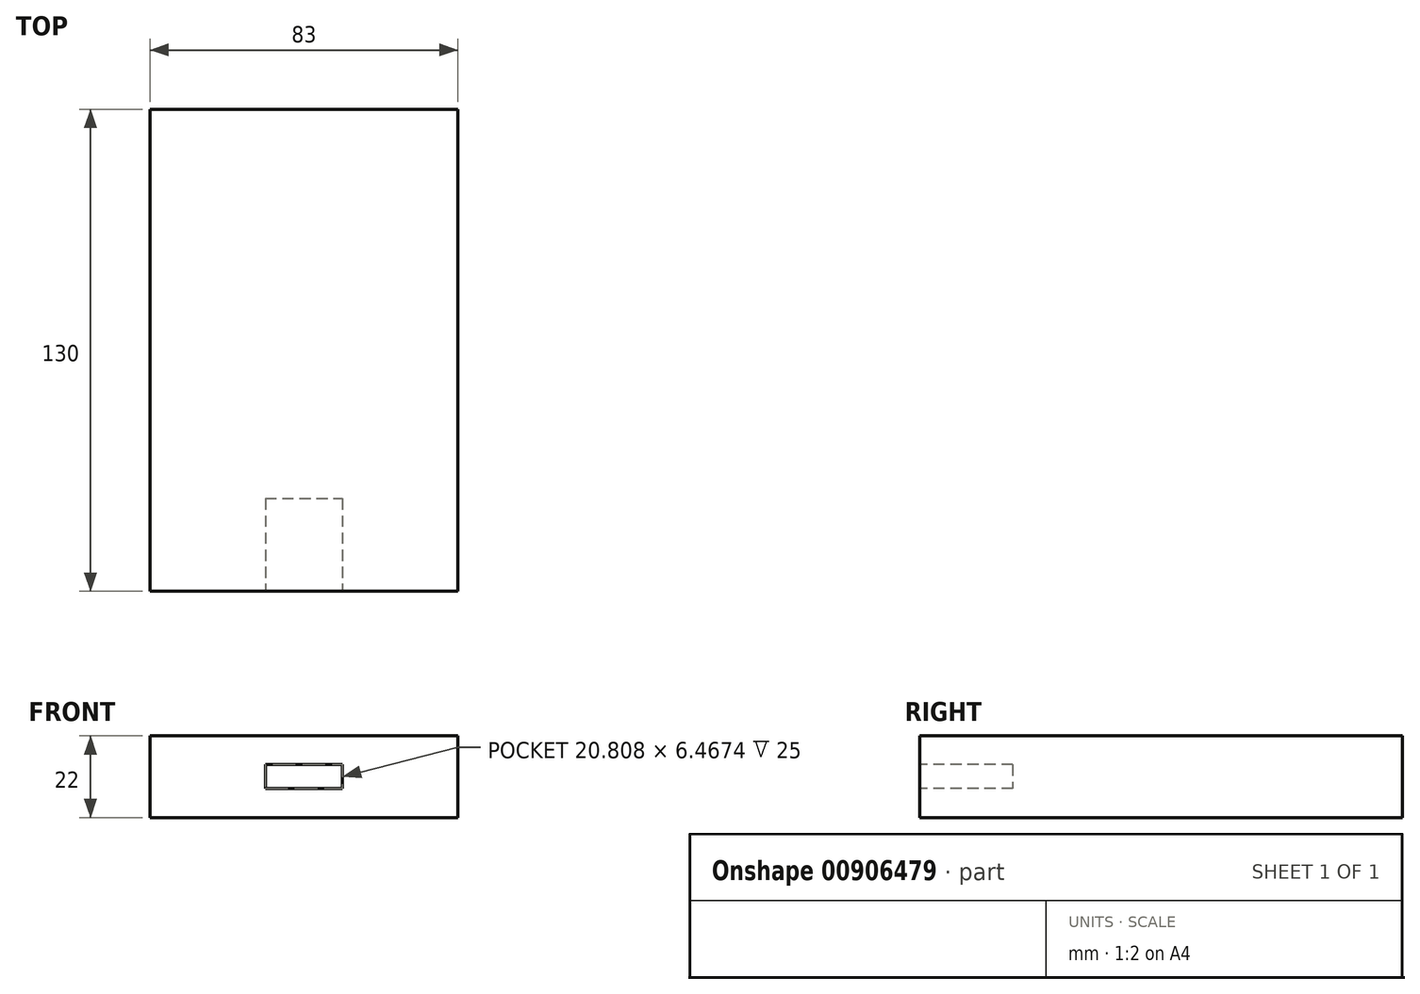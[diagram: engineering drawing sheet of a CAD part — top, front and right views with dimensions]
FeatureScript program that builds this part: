
annotation { "Feature Type Name" : "Feature", "Feature Type Description" : "" }
export const myFeature = defineFeature(function(context is Context, id is Id, definition is map)
    precondition{}
    {
        {
            var Q0;
            Q0=qCreatedBy(makeId("Top.planeOp"),FACE);
            var sketch = newSketch(context, id + "F0", { "sketchPlane" : qUnion([Q0])});
            skLineSegment(sketch, "E0.bottom", {"start": v(-41.5, 65) * mm, "end": v(41.5, 65) * mm});
            skLineSegment(sketch, "E0.top", {"start": v(-41.5, -65) * mm, "end": v(41.5, -65) * mm});
            skLineSegment(sketch, "E0.left", {"start": v(-41.5, 65) * mm, "end": v(-41.5, -65) * mm});
            skLineSegment(sketch, "E0.right", {"start": v(41.5, 65) * mm, "end": v(41.5, -65) * mm});
            skPoint(sketch, "E0.middle", {"position": v(0, 0) * mm});
            skSolve(sketch);
        }
        {
            var Q0;
            Q0=makeQuery(id+"F0.imprint","IMPRINT",FACE,{"disambiguationData":[TD([[makeQuery(id+"F0.imprint","IMPRINT",EDGE,{"derivedFrom":sQuery(id+"F0.wireOp",EDGE,"E0.bottom")}),-1.0]])]});
            extrude(context, id + "F1", {"entities" : qUnion([Q0]), "depth" : 22 * mm, "offsetDistance" : 25 * mm});
        }
        {
            var Q0;
            Q0=makeQuery(id+"F1.opExtrude","SWEPT_FACE",FACE,{"disambiguationData":[OSD([sQuery(id+"F0.wireOp",EDGE,"E0.top")])]});
            var sketch = newSketch(context, id + "F2", { "sketchPlane" : qUnion([Q0])});
            skLineSegment(sketch, "E1.bottom", {"start": v(-10.4, 14.23) * mm, "end": v(10.4, 14.23) * mm});
            skLineSegment(sketch, "E1.top", {"start": v(-10.4, 7.77) * mm, "end": v(10.4, 7.77) * mm});
            skLineSegment(sketch, "E1.left", {"start": v(-10.4, 14.23) * mm, "end": v(-10.4, 7.77) * mm});
            skLineSegment(sketch, "E1.right", {"start": v(10.4, 14.23) * mm, "end": v(10.4, 7.77) * mm});
            skPoint(sketch, "E1.middle", {"position": v(0, 11) * mm});
            skPoint(sketch, "E1.middle.positionSnap0", {"position": v(41.5, 11) * mm});
            skPoint(sketch, "E1.middle.positionSnap1", {"position": v(0, 22) * mm});
            skPoint(sketch, "E1.centerSnap0", {"position": v(41.5, 11) * mm});
            skPoint(sketch, "E1.centerSnap1", {"position": v(0, 22) * mm});
            skSolve(sketch);
        }
        {
            var Q0;
            Q0=makeQuery(id+"F2.imprint","IMPRINT",FACE,{"disambiguationData":[TD([[makeQuery(id+"F2.imprint","IMPRINT",EDGE,{"derivedFrom":sQuery(id+"F2.wireOp",EDGE,"E1.bottom")}),-1.0]])]});
            extrude(context, id + "F3", {"entities" : qUnion([Q0]), "operationType" : NewBodyOperationType.REMOVE, "oppositeDirection" : true, "depth" : 25 * mm, "offsetDistance" : 25 * mm});
        }
    });
